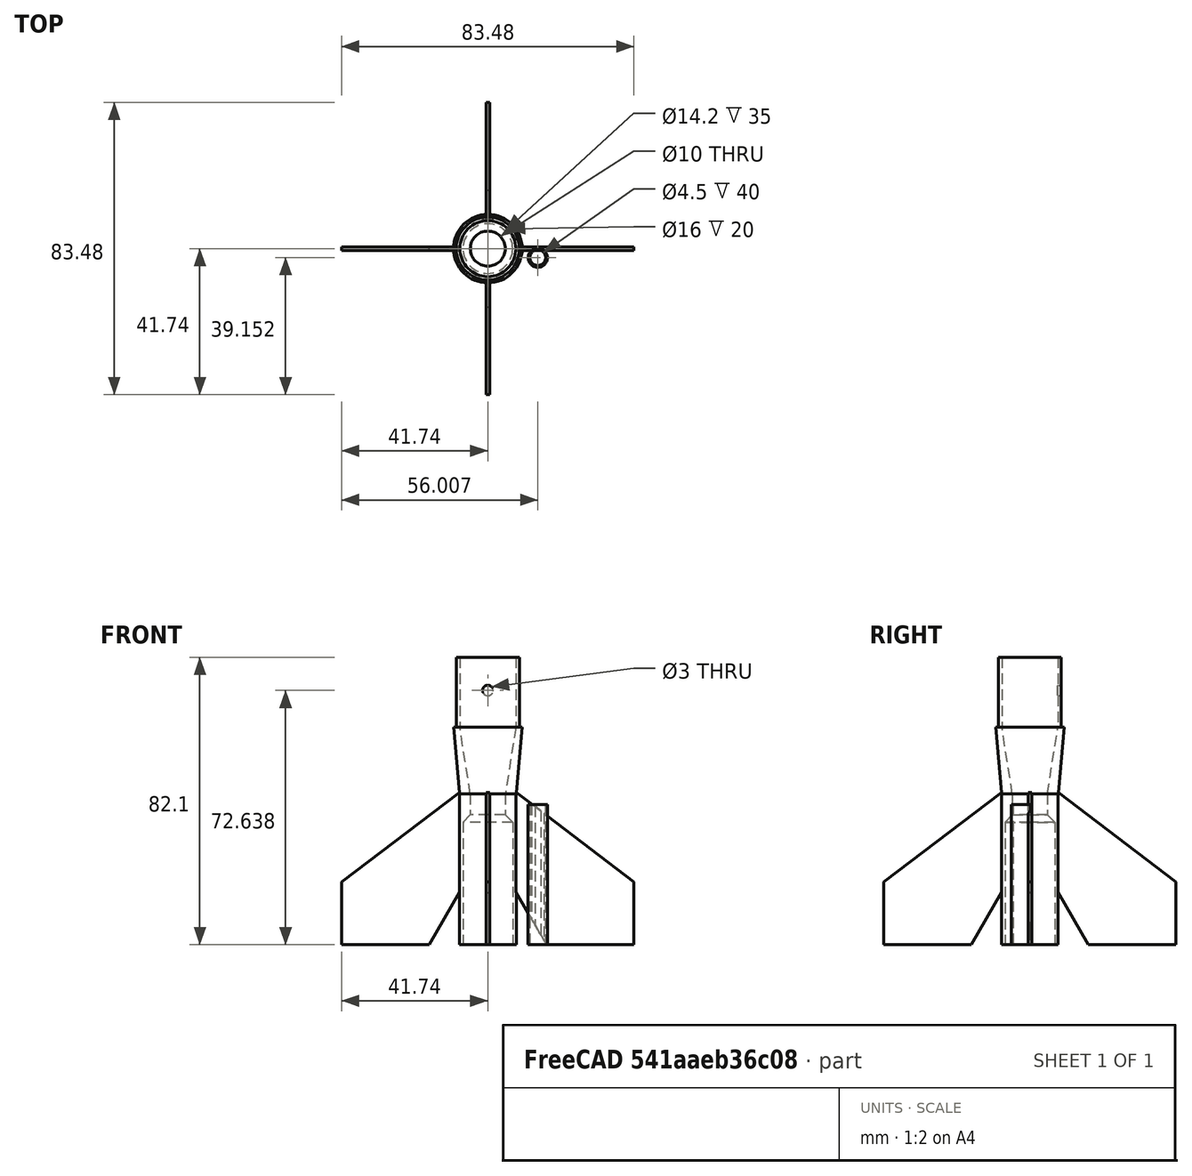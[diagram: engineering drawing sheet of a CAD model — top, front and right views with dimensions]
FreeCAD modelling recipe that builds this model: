
FCSTD DOCUMENT  (FreeCAD 0.20R29603 (Git))
Label: Ez3D Mini Lite Fin Can
License: All rights reserved
LicenseURL: http://en.wikipedia.org/wiki/All_rights_reserved
objects: Sketcher::SketchObject×4, PartDesign::Pad×2, PartDesign::Revolution×1, PartDesign::PolarPattern×1, PartDesign::Plane×1, PartDesign::Hole×1, PartDesign::Body×1, Mesh::Feature×1
note: 15 computed .brp shape members not serialized (recipe doc carries the construction recipe); baked Part::Feature solids carry a one-line shape summary decoded from their .brp

FEATURE [Sketcher::SketchObject] Sketch  label="Fin Can and Transition"
  FullyConstrained = true
  MapMode = 5
  Placement = pos=(0,0,0) rot=(1,0,0;1.5708rad)
  Support = -> [XZ_Plane]
  sketch-geometry (11):
    g0: LineSegment StartX=7.1 StartY=0 StartZ=0 EndX=8.1 EndY=0 EndZ=0
    g1: LineSegment StartX=8.1 StartY=0 StartZ=0 EndX=8.1 EndY=43.1 EndZ=0
    g2: LineSegment StartX=5 StartY=43.1 StartZ=0 EndX=5 EndY=37.1 EndZ=0
    g3: LineSegment StartX=5 StartY=37.1 StartZ=0 EndX=7.1 EndY=35 EndZ=0
    g4: LineSegment StartX=7.1 StartY=35 StartZ=0 EndX=7.1 EndY=0 EndZ=0
    g5: LineSegment StartX=8.1 StartY=43.1 StartZ=0 EndX=9.8 EndY=62.1 EndZ=0
    g6: LineSegment StartX=8 StartY=82.1 StartZ=0 EndX=8 EndY=62.1 EndZ=0
    g7: LineSegment StartX=8 StartY=62.1 StartZ=0 EndX=5 EndY=43.1 EndZ=0
    g8: LineSegment StartX=9.8 StartY=62.1 StartZ=0 EndX=9 EndY=62.1 EndZ=0
    g9: LineSegment StartX=9 StartY=62.1 StartZ=0 EndX=9 EndY=82.1 EndZ=0
    g10: LineSegment StartX=9 StartY=82.1 StartZ=0 EndX=8 EndY=82.1 EndZ=0
  constraints (33):
    c: PointOnObject(g0,g-1)
    c: PointOnObject(g0,g-1)
    c: Coincident(g0,g1)
    c: Vertical(g1)
    c: Vertical(g2)
    c: Coincident(g2,g3)
    c: Coincident(g3,g4)
    c: Coincident(g4,g0)
    c: Vertical(g4)
    c: DistanceX(g0,g0) = 1
    c: DistanceX(g-1,g0) = 7.1
    c: DistanceY(g0,g3) = 35
    c: Angle(g3) = -0.785398
    c: DistanceX(g-1,g2) = 5
    c: Coincident(g1,g5)
    c: Vertical(g6)
    c: Coincident(g6,g7)
    c: Coincident(g2,g7)
    c: Coincident(g5,g8)
    c: Coincident(g8,g9)
    c: Vertical(g9)
    c: Coincident(g9,g10)
    c: Coincident(g10,g6)
    c: Horizontal(g10)
    c: Horizontal(g8)
    c: DistanceX(g-1,g9) = 9
    c: DistanceX(g10,g10) = 1
    c: DistanceY(g2,g2) = 6
    c: DistanceY(g2,g6) = 19
    c: Horizontal(g6,g8)
    c: DistanceY(g6,g6) = 20
    c: Horizontal(g2,g1)
    c: DistanceX(g8,g5) = 0.8
FEATURE [PartDesign::Revolution] Revolution  label="Revolution for Fin Can"
  Angle = 360
  Axis = (0,-2e-16,1)
  Base = (0,0,0)
  Placement = pos=(0,0,0) rot=(1,0,0;1.5708rad)
  Profile = -> Sketch
  ReferenceAxis = -> Sketch [V_Axis]
  Reversed = true
FEATURE [Sketcher::SketchObject] Sketch001  label="Fin"
  FullyConstrained = true
  MapMode = 5
  Placement = pos=(0,0,0) rot=(1,0,0;1.5708rad)
  Support = -> [XZ_Plane]
  sketch-geometry (5):
    g0: LineSegment StartX=16.7376 StartY=0 StartZ=0 EndX=41.7376 EndY=0 EndZ=0
    g1: LineSegment StartX=41.7376 StartY=0 StartZ=0 EndX=41.7376 EndY=18 EndZ=0
    g2: LineSegment StartX=41.7376 StartY=18 StartZ=0 EndX=7.5 EndY=44 EndZ=0
    g3: LineSegment StartX=7.5 StartY=44 StartZ=0 EndX=7.5 EndY=16 EndZ=0
    g4: LineSegment StartX=7.5 StartY=16 StartZ=0 EndX=16.7376 EndY=0 EndZ=0
  constraints (15):
    c: Horizontal(g0)
    c: Coincident(g0,g1)
    c: Coincident(g1,g2)
    c: Vertical(g1)
    c: Coincident(g2,g3)
    c: Vertical(g3)
    c: Coincident(g3,g4)
    c: Coincident(g0,g4)
    c: DistanceX(g-1,g2) = 7.5
    c: Angle(g4) = -1.0472
    c: PointOnObject(g0,g-1)
    c: DistanceY(g1,g1) = 18
    c: DistanceX(g0,g0) = 25
    c: DistanceY(g3,g3) = 28
    c: DistanceY(g0,g2) = 44
FEATURE [PartDesign::Pad] Pad  label="Fin 1mm thick"
  BaseFeature = -> Revolution
  Direction = (0,-1,-2e-16)
  Length = 1
  Length2 = 100
  Midplane = true
  Placement = pos=(0,0,0) rot=(1,0,0;1.5708rad)
  Profile = -> Sketch001
  ReferenceAxis = -> Sketch001 [N_Axis]
  Type = 0
FEATURE [PartDesign::PolarPattern] PolarPattern  label="Add Multiple Fins"
  Angle = 360
  Axis = -> Z_Axis
  BaseFeature = -> Pad
  Occurrences = 4
  Originals = -> [Pad]
  Placement = pos=(0,0,0) rot=(1,0,0;1.5708rad)
FEATURE [Sketcher::SketchObject] Sketch002  label="Launch Lug 4.5mm ID 5.5mm OD"
  FullyConstrained = false
  MapMode = 5
  Support = -> [XY_Plane]
  sketch-geometry (2):
    g0: Circle CenterX=14.2672 CenterY=-2.58802 CenterZ=0 NormalX=0 NormalY=0 NormalZ=1 AngleXU=0 Radius=2.75
    g1: Circle CenterX=14.2672 CenterY=-2.58802 CenterZ=0 NormalX=0 NormalY=0 NormalZ=1 AngleXU=0 Radius=2.25
  constraints (4):
    c: Coincident(g1,g0)
    c: Diameter(g0) = 5.5
    c: Diameter(g1) = 4.5
    c: Distance(g-1,g0) = 14.5
FEATURE [PartDesign::Pad] Pad001  label="Launch Lug 40mm long"
  BaseFeature = -> PolarPattern
  Direction = (0,0,1)
  Length = 40
  Length2 = 100
  Placement = pos=(0,0,0) rot=(1,0,0;1.5708rad)
  Profile = -> Sketch002
  ReferenceAxis = -> Sketch002 [N_Axis]
  Type = 0
FEATURE [PartDesign::Plane] DatumPlane  label="DatumPlane for Recovery Harness Hole"
  Length = 102.386
  MapMode = 5
  Placement = pos=(0,-0.5,0) rot=(1,0,0;1.5708rad)
  ResizeMode = 0
  Support = -> [Pad001]
  Width = 126.011
FEATURE [Sketcher::SketchObject] Sketch003  label="Recovery Harness Hole"
  FullyConstrained = false
  MapMode = 5
  Placement = pos=(0,-0.5,0) rot=(1,0,0;1.5708rad)
  Support = -> [DatumPlane]
  sketch-geometry (1):
    g0: Circle CenterX=0 CenterY=72.6377 CenterZ=0 NormalX=0 NormalY=0 NormalZ=1 AngleXU=0 Radius=1.56488
  constraints (1):
    c: PointOnObject(g0,g-2)
FEATURE [PartDesign::Hole] Hole  label="3mm hole for recovery harness"
  BaseFeature = -> Pad001
  CustomThreadClearance = 0
  Depth = 25
  DepthType = 0
  Diameter = 3
  DrillForDepth = false
  DrillPoint = 1
  DrillPointAngle = 118
  HoleCutCountersinkAngle = 90
  HoleCutCustomValues = false
  HoleCutDepth = 0
  HoleCutDiameter = 6.1
  HoleCutType = 0
  ModelThread = false
  Placement = pos=(0,0,0) rot=(1,0,0;1.5708rad)
  Profile = -> Sketch003
  Tapered = false
  TaperedAngle = 90
  ThreadClass = 0
  ThreadDepth = 25
  ThreadDepthType = 0
  ThreadDirection = 0
  ThreadFit = 0
  ThreadSize = 0
  ThreadType = 0
  Threaded = false
  UseCustomThreadClearance = false
FEATURE [PartDesign::Body] Body
  Group = -> [Sketch,Revolution,Sketch001,Pad,PolarPattern,Sketch002,Pad001,DatumPlane,Sketch003,Hole]
  Origin = -> Origin
  Tip = -> Hole
FEATURE [Mesh::Feature] _3mmThread20x2_5_5mmTall  label="13mmThread20x2.5-5mmTall"
